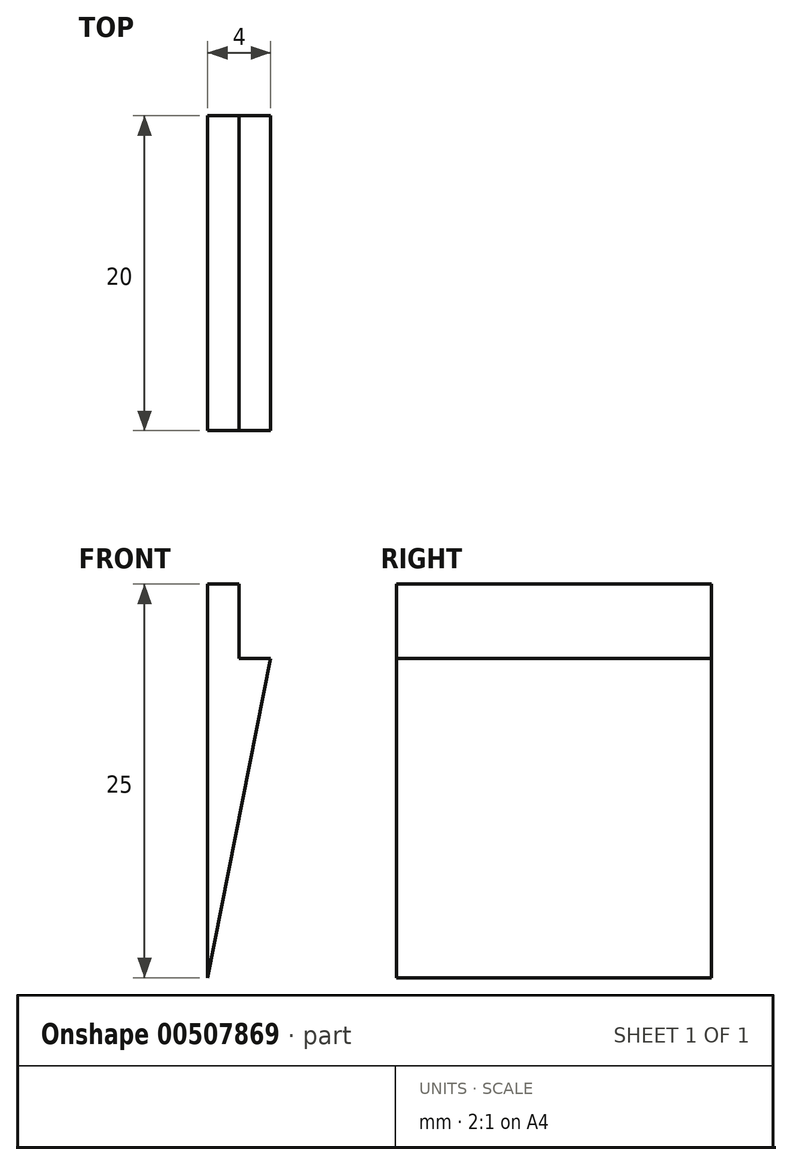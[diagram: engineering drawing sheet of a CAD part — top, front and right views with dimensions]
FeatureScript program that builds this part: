
annotation { "Feature Type Name" : "Feature", "Feature Type Description" : "" }
export const myFeature = defineFeature(function(context is Context, id is Id, definition is map)
    precondition{}
    {
        {
            var Q0;
            Q0=qCreatedBy(makeId("Front.planeOp"),FACE);
            var sketch = newSketch(context, id + "F0", { "sketchPlane" : qUnion([Q0])});
            skLineSegment(sketch, "E0", {"start": v(0, 0) * mm, "end": v(0, 25) * mm});
            skLineSegment(sketch, "E1", {"start": v(0, 25) * mm, "end": v(2, 25) * mm});
            skLineSegment(sketch, "E2", {"start": v(2, 25) * mm, "end": v(2, 20.28) * mm});
            skLineSegment(sketch, "E3", {"start": v(2, 20.28) * mm, "end": v(4, 20.28) * mm});
            skLineSegment(sketch, "E4", {"start": v(4, 20.28) * mm, "end": v(0, 0) * mm});
            skSolve(sketch);
        }
        {
            var Q0;
            Q0=makeQuery(id+"F0.imprint","IMPRINT",FACE,{"disambiguationData":[TD([[makeQuery(id+"F0.imprint","IMPRINT",EDGE,{"derivedFrom":sQuery(id+"F0.wireOp",EDGE,"E0")}),-1.0]])]});
            extrude(context, id + "F1", {"entities" : qUnion([Q0]), "depth" : 20 * mm});
        }
    });
